# Revit family: Hager-Univers-IP44-D205-H1250-Cl.II-Encl-PL-pl
name_source: partatom
category: Equipement électrique
units: mm (PartAtom-declared; Revit-internal decimal feet)

## family parameters
Configuration du panneau = Deux colonnes, circuits au sein
Cote de connecteur circulaire = Utiliser le diamètre
Couper avec des vides une fois chargée = Non
Hôte = Face
Partagée = Non
Point de calcul de pièce = Non
Type d'élément = Tableau de raccordement

## types (5) — shared parameters
Commentaires du type = Univers
EF000003 - Sposób montażu = EV000384 - Montaż natynkowy
EF000007 - Kolor = EV000202 - Biały
EF000040 - Wysokość = 1250 mm  [stored 4.10105 ft]
EF000049 - Głębokość = 205 mm  [stored 0.672572 ft]
EF000116 - Numer RAL = 9010
EF000118 - Z płytą montażową = Non
EF000218 - Głębokość wbudowania = 205 mm  [stored 0.672572 ft]
EF000266 - Liczba rzędów = 8
EF001088 - Możliwość rozbudowy = Oui
EF001596 - Materiał obudowy = EV000179 - Stal
EF001613 - Podtrzymanie funkcji = EV000494 - Brak
EF003532 - Do zastosowań zewnętrznych = Non
EF004293 - Odporność udarowa = EV006815 - IK09
EF005474 - Stopień ochrony (IP) = EV006418 - IP44
EF006244 - Transparentna pokrywa/drzwi = Non
EF006306 - Z zamkiem = Non
EF007800 - Do ochrony odgromowej = Non
EF008873 - Prąd znamionowy (In) = 250 A
EF009170 - Obudowa z materiału o wysokiej wytrzymałości mechanicznej = 1 mm  [stored 0.00328084 ft]
EF009171 - Drzwi/pokrywa z materiału o wysokiej wytrzymałości mechanicznej = 1 mm  [stored 0.00328084 ft]
EF009212 - Wykonanie pokrywy = EV000116 - Zamknięty
EF015940 - Pokrywa z wyzwalaczem nadciśnieniowym = Non
Fabricant = Hager
HG000002 - Z drzwiami lub pokrywą = Oui
HG000003 - Zakres = Univers
HG000006 - Montaż podtynkowy = Non
HG000023 - Obudowa dwusekcyjna = Non
HG000024 - Wysokość części dolnej = 800 mm  [stored 2.62467 ft]
HG000026 - Stojąca = Non
zero-valued in all types: Elévation par défaut, HG000027 - Wysokość cokołu

## per-type parameters (varying)
| type | EF000008 - Szerokość | EF000339 - Rodzaj pokrywy | EF000437 - Liczba wejść kablowych | EF001131 - Głębokość wewnętrzna | EF002950 - Szerokość wyrażona liczbą modułów | EF004427 - Liczba modułów | EF004464 - Rodzaj drzwi | EF009554 - Liczba otworów pod flansze | HG000004 - Referencja producenta | HG000009 - Drzwi dwuskrzydłowe | HG000010 - Drzwi asymetryczne |
| Montaż natynkowy IP44 S1050 W1250 G205  - FP84SN2 | 1050 mm | EV004216 - Drzwi | 8 | 130 mm  [stored 0.426509 ft] | 48 | 384 | EV003602 - Podwójny | 8 | FP84SN2 | Oui | Non |
| Montaż natynkowy IP44 S1300 W1250 G205  - FP85SN2 | 1300 mm  [stored 4.26509 ft] | EV004216 - Drzwi | 10 | 130 mm  [stored 0.426509 ft] | 60 | 480 | EV003602 - Podwójny | 10 | FP85SN2 | Oui | Oui |
| Montaż natynkowy IP44 S300 W1250 G205  - FP81SN2 | 300 mm | EV001012 - Pokrywa | 2 | 143 mm | 12 | 96 | EV002646 - Pojedynczy | 2 | FP81SN2 | Non | Non |
| Montaż natynkowy IP44 S550 W1250 G205  - FP82SN2 | 550 mm | EV001012 - Pokrywa | 4 | 143 mm | 24 | 192 | EV002646 - Pojedynczy | 4 | FP82SN2 | Non | Non |
| Montaż natynkowy IP44 S800 W1250 G205  - FP83SN2 | 800 mm  [stored 2.62467 ft] | EV004216 - Drzwi | 6 | 130 mm  [stored 0.426509 ft] | 36 | 288 | EV002646 - Pojedynczy | 6 | FP83SN2 | Non | Non |

note: [stored X ft] marks values corroborated as IEEE doubles in the binary element streams (Revit-internal decimal feet)

## geometry (parser evidence)
native form markers: Sweep x10
no freeform markers — native parametric forms only
